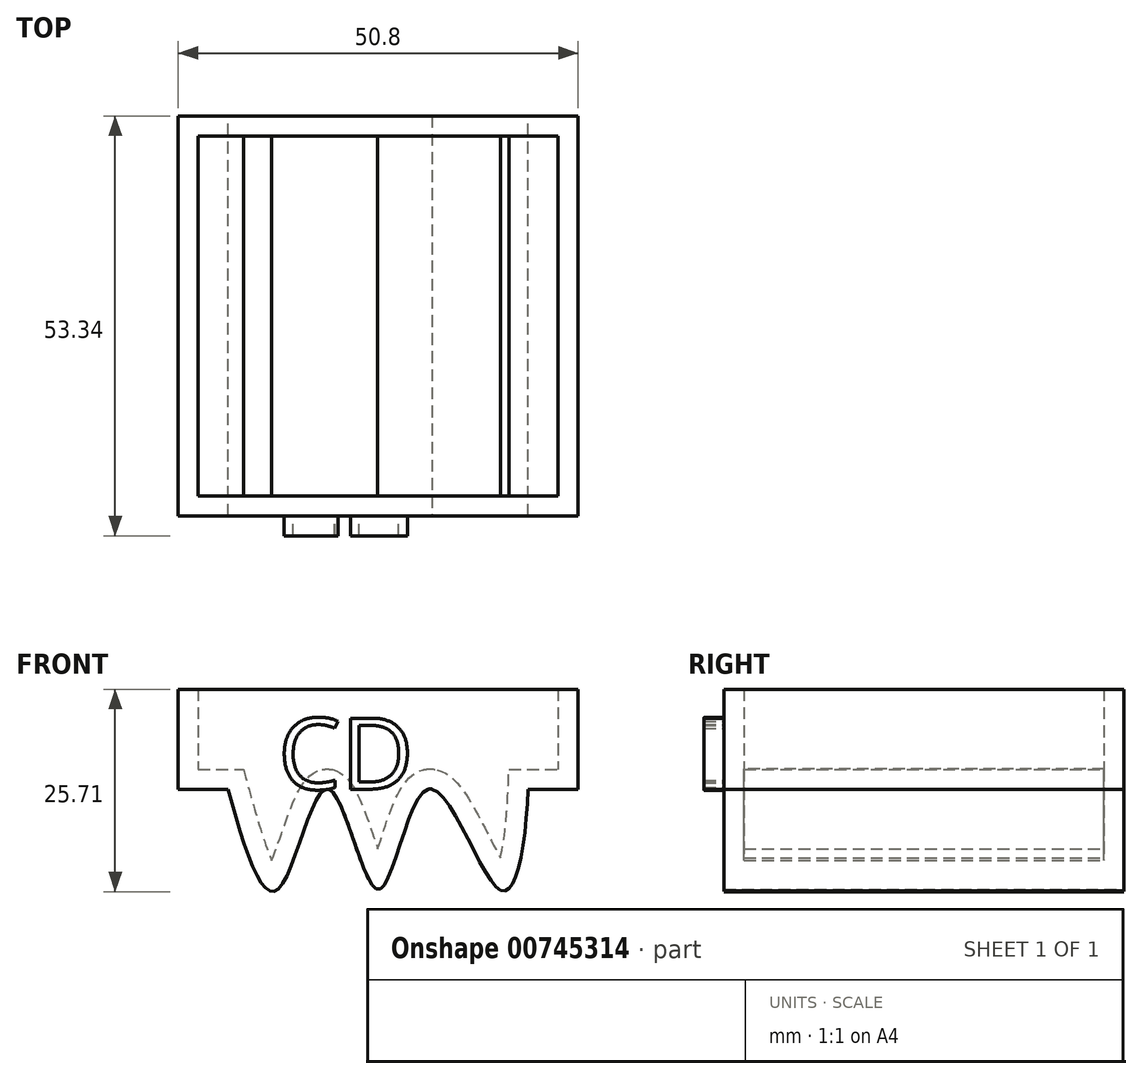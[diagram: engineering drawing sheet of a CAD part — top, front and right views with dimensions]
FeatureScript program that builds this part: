
annotation { "Feature Type Name" : "Feature", "Feature Type Description" : "" }
export const myFeature = defineFeature(function(context is Context, id is Id, definition is map)
    precondition{}
    {
        {
            var Q0;
            Q0=qCreatedBy(makeId("Front.planeOp"),FACE);
            var sketch = newSketch(context, id + "F0", { "sketchPlane" : qUnion([Q0])});
            skLineSegment(sketch, "E0.bottom", {"start": v(-63.36, 22.42) * mm, "end": v(-12.56, 22.42) * mm});
            skLineSegment(sketch, "E0.left", {"start": v(-63.36, 22.42) * mm, "end": v(-63.36, 9.72) * mm});
            skLineSegment(sketch, "E0.right", {"start": v(-12.56, 22.42) * mm, "end": v(-12.56, 9.72) * mm});
            skLineSegment(sketch, "E1", {"start": v(-63.36, 9.72) * mm, "end": v(-57.01, 9.72) * mm});
            skFitSpline(sketch, "E2", {"points": [v(-57.01, 9.72) * mm, v(-50.66, -2.98) * mm, v(-44.31, 9.72) * mm, v(-37.96, -2.98) * mm, v(-31.61, 9.72) * mm, v(-22.63, -2.98) * mm, v(-18.91, 9.72) * mm], "startDerivative": vector(35.4, -130.63) * mm, "endDerivative": vector(5.62, 134.56) * mm});
            skPoint(sketch, "E3.orphan", {"position": v(-63.36, -2.98) * mm});
            skPoint(sketch, "E4.orphan", {"position": v(-12.56, -2.98) * mm});
            skLineSegment(sketch, "E5.trimOffspring", {"start": v(-18.91, 9.72) * mm, "end": v(-12.56, 9.72) * mm});
            skLineSegment(sketch, "E6.trimOffspring", {"start": v(-31.61, 9.72) * mm, "end": v(-31.1, 9.72) * mm});
            skLineSegment(sketch, "E7.trimOffspring", {"start": v(-44.57, 9.72) * mm, "end": v(-44.31, 9.72) * mm});
            skSolve(sketch);
        }
        {
            var Q0;
            Q0=makeQuery(id+"F0.imprint","IMPRINT",FACE,{"disambiguationData":[TD([[makeQuery(id+"F0.imprint","IMPRINT",EDGE,{"derivedFrom":sQuery(id+"F0.wireOp",EDGE,"E0.bottom")}),-1.0]])]});
            extrude(context, id + "F1", {"entities" : qUnion([Q0]), "depth" : 50.8 * mm, "offsetDistance" : 25.4 * mm});
        }
        {
            var Q0;
            Q0=makeQuery(id+"F1.opExtrude","SWEPT_FACE",FACE,{"disambiguationData":[OSD([sQuery(id+"F0.wireOp",EDGE,"E0.bottom")])]});
            shell(context, id + "F2", {"entities" : qUnion([Q0]), "thickness" : 2.54 * mm});
        }
        {
            var Q0;
            Q0=makeQuery(id+"F1.opExtrude","CAP_FACE",FACE,{"disambiguationData":[OSD([sQuery(id+"F0.wireOp",EDGE,"E0.bottom"),sQuery(id+"F0.wireOp",EDGE,"E0.left"),sQuery(id+"F0.wireOp",EDGE,"E0.right"),sQuery(id+"F0.wireOp",EDGE,"E1"),sQuery(id+"F0.wireOp",EDGE,"E2"),sQuery(id+"F0.wireOp",EDGE,"E5.trimOffspring")])],"isStart":false});
            var sketch = newSketch(context, id + "F3", { "sketchPlane" : qUnion([Q0])});
            skText(sketch, "E8", { "text": "CD", "fontName": "OpenSans-Regular.ttf"});
            const initialGuessF3  = {"E8": [-0.05066, 0.00972, 1, 0, 0.0091]};
            skSetInitialGuess(sketch, initialGuessF3);
            skSolve(sketch);
        }
        {
            var Q0;
            Q0 = qSketchRegion(id + "F3", true);
            extrude(context, id + "F4", {"entities" : qUnion([Q0]), "operationType" : NewBodyOperationType.ADD, "depth" : 2.54 * mm, "offsetDistance" : 25.4 * mm});
        }
    });
